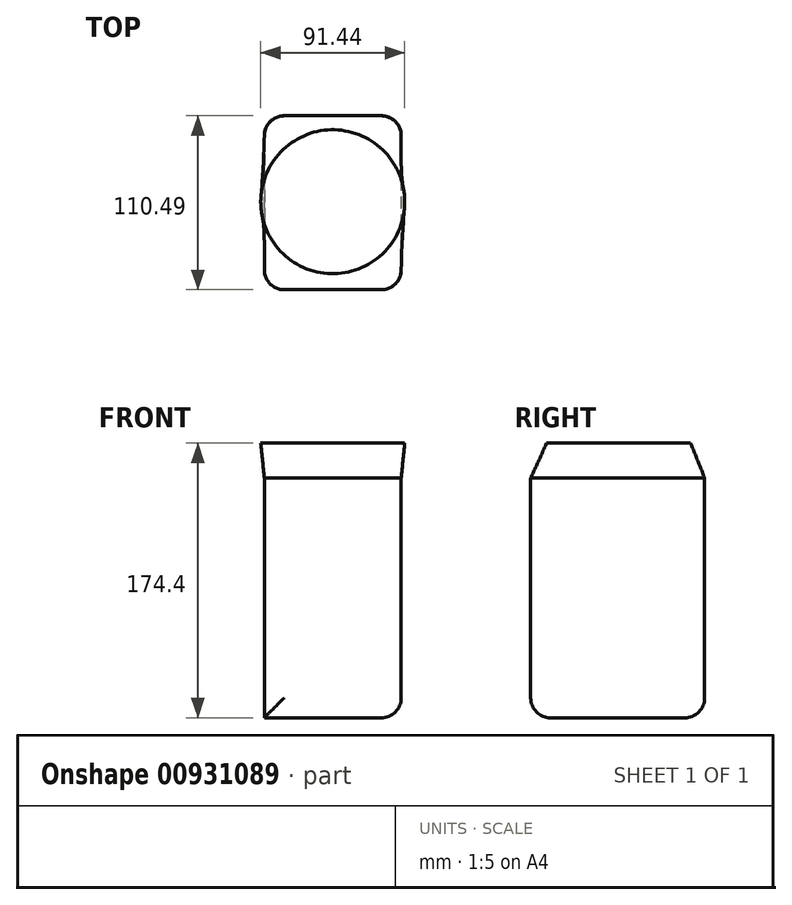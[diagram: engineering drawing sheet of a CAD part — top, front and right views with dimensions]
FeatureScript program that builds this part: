
annotation { "Feature Type Name" : "Feature", "Feature Type Description" : "" }
export const myFeature = defineFeature(function(context is Context, id is Id, definition is map)
    precondition{}
    {
        {
            var Q0;
            Q0=qCreatedBy(makeId("Top.planeOp"),FACE);
            var sketch = newSketch(context, id + "F0", { "sketchPlane" : qUnion([Q0])});
            skLineSegment(sketch, "E0.bottom", {"start": v(-46.02, 77.78) * mm, "end": v(40.92, 77.78) * mm});
            skLineSegment(sketch, "E0.top", {"start": v(-46.02, -32.71) * mm, "end": v(40.92, -32.71) * mm});
            skLineSegment(sketch, "E0.left", {"start": v(-46.02, 77.78) * mm, "end": v(-46.02, -32.71) * mm});
            skLineSegment(sketch, "E0.right", {"start": v(40.92, 77.78) * mm, "end": v(40.92, -32.71) * mm});
            skSolve(sketch);
        }
        {
            var Q0;
            Q0=makeQuery(id+"F0.imprint","IMPRINT",FACE,{"disambiguationData":[TD([[makeQuery(id+"F0.imprint","IMPRINT",EDGE,{"derivedFrom":sQuery(id+"F0.wireOp",EDGE,"E0.bottom")}),-1.0]])]});
            extrude(context, id + "F1", {"entities" : qUnion([Q0]), "depth" : 152.4 * mm, "offsetDistance" : 25.4 * mm});
        }
        {
            var Q0;
            Q0=makeQuery(id+"F1.opExtrude","CAP_FACE",FACE,{"disambiguationData":[OSD([sQuery(id+"F0.wireOp",EDGE,"E0.bottom"),sQuery(id+"F0.wireOp",EDGE,"E0.top"),sQuery(id+"F0.wireOp",EDGE,"E0.left"),sQuery(id+"F0.wireOp",EDGE,"E0.right")])],"isStart":false});
            var sketch = newSketch(context, id + "F2", { "sketchPlane" : qUnion([Q0])});
            skLineSegment(sketch, "E1.bottom", {"start": v(-33.32, 77.78) * mm, "end": v(28.22, 77.78) * mm});
            skLineSegment(sketch, "E1.top", {"start": v(-33.32, -32.71) * mm, "end": v(28.22, -32.71) * mm});
            skLineSegment(sketch, "E1.left", {"start": v(-46.02, 65.08) * mm, "end": v(-46.02, -20.01) * mm});
            skLineSegment(sketch, "E1.right", {"start": v(40.92, 65.08) * mm, "end": v(40.92, -20.01) * mm});
            skPoint(sketch, "E2.visualSharp", {"position": v(-46.02, -32.71) * mm});
            skArc(sketch, "E2.filletArc", {"start": v(-46.02, -20.01) * mm, "mid": v(-42.3, -29) * mm, "end": v(-33.32, -32.71) * mm});
            skPoint(sketch, "E3.visualSharp", {"position": v(-46.02, 77.78) * mm});
            skArc(sketch, "E3.filletArc", {"start": v(-33.32, 77.78) * mm, "mid": v(-42.3, 74.06) * mm, "end": v(-46.02, 65.08) * mm});
            skPoint(sketch, "E4.visualSharp", {"position": v(40.92, -32.71) * mm});
            skArc(sketch, "E4.filletArc", {"start": v(28.22, -32.71) * mm, "mid": v(37.2, -29) * mm, "end": v(40.92, -20.01) * mm});
            skPoint(sketch, "E5.visualSharp", {"position": v(40.92, 77.78) * mm});
            skArc(sketch, "E5.filletArc", {"start": v(40.92, 65.08) * mm, "mid": v(37.2, 74.06) * mm, "end": v(28.22, 77.78) * mm});
            skSolve(sketch);
        }
        {
            var Q0;
            Q0=makeQuery(id+"F1.opExtrude","SWEPT_EDGE",EDGE,{"disambiguationData":[OSD([sQuery(id+"F0.wireOp",EDGE,"E0.bottom"),sQuery(id+"F0.wireOp",EDGE,"E0.right")])]});
            var Q1;
            Q1=makeQuery(id+"F1.opExtrude","CAP_EDGE",EDGE,{"disambiguationData":[OSD([sQuery(id+"F0.wireOp",EDGE,"E0.right")])],"isStart":true});
            var Q2;
            Q2=makeQuery(id+"F1.opExtrude","SWEPT_EDGE",EDGE,{"disambiguationData":[OSD([sQuery(id+"F0.wireOp",EDGE,"E0.top"),sQuery(id+"F0.wireOp",EDGE,"E0.right")])]});
            var Q3;
            Q3=makeQuery(id+"F1.opExtrude","SWEPT_EDGE",EDGE,{"disambiguationData":[OSD([sQuery(id+"F0.wireOp",EDGE,"E0.bottom"),sQuery(id+"F0.wireOp",EDGE,"E0.left")])]});
            var Q4;
            Q4=makeQuery(id+"F1.opExtrude","CAP_EDGE",EDGE,{"disambiguationData":[OSD([sQuery(id+"F0.wireOp",EDGE,"E0.bottom")])],"isStart":true});
            var Q5;
            Q5=makeQuery(id+"F1.opExtrude","CAP_EDGE",EDGE,{"disambiguationData":[OSD([sQuery(id+"F0.wireOp",EDGE,"E0.top")])],"isStart":true});
            var Q6;
            Q6=makeQuery(id+"F1.opExtrude","SWEPT_EDGE",EDGE,{"disambiguationData":[OSD([sQuery(id+"F0.wireOp",EDGE,"E0.top"),sQuery(id+"F0.wireOp",EDGE,"E0.left")])]});
            fillet(context, id + "F3", {"entities" : qUnion([Q0, Q1, Q2, Q3, Q4, Q5, Q6]), "radius" : 12.7 * mm, "tangentPropagation" : true, "allowEdgeOverflow" : false});
        }
        {
            var Q0;
            Q0=makeQuery(id+"F2.imprint","IMPRINT",FACE,{"disambiguationData":[TD([[makeQuery(id+"F2.imprint","IMPRINT",EDGE,{"derivedFrom":sQuery(id+"F2.wireOp",EDGE,"E1.bottom")}),-1.0]])]});
            cPlane(context, id + "F4", {"entities" : qUnion([Q0]), "cplaneType" : CPlaneType.OFFSET, "offset" : 22 * mm, "width" : 152.4 * mm, "height" : 152.4 * mm});
        }
        {
            var Q0;
            Q0=qCreatedBy(id+"F4.planeOp",FACE);
            var sketch = newSketch(context, id + "F5", { "sketchPlane" : qUnion([Q0])});
            skPoint(sketch, "E6.positionSnap0", {"position": v(40, 23.15) * mm});
            skCircle(sketch, "E7", {"center": v(-2.55, 23.15) * mm, "radius": 45.72 * mm});
            skPoint(sketch, "E7.centerSnap0", {"position": v(-2.55, 77.22) * mm});
            skSolve(sketch);
        }
        {
            var Q1;
            Q1=makeQuery(id+"F2.imprint","IMPRINT",FACE,{"disambiguationData":[TD([[makeQuery(id+"F2.imprint","IMPRINT",EDGE,{"derivedFrom":sQuery(id+"F2.wireOp",EDGE,"E1.bottom")}),-1.0]])]});
            var Q2;
            Q2=makeQuery(id+"F5.imprint","IMPRINT",FACE,{"disambiguationData":[TD([[makeQuery(id+"F5.imprint","IMPRINT",EDGE,{"derivedFrom":sQuery(id+"F5.wireOp",EDGE,"E7")}),1.0]])]});
            loft(context, id + "F6", {"operationType" : NewBodyOperationType.ADD, "sheetProfilesArray" : [{ "sheetProfileEntities" : qUnion([Q1]) }, { "sheetProfileEntities" : qUnion([Q2]) }]});
        }
    });
